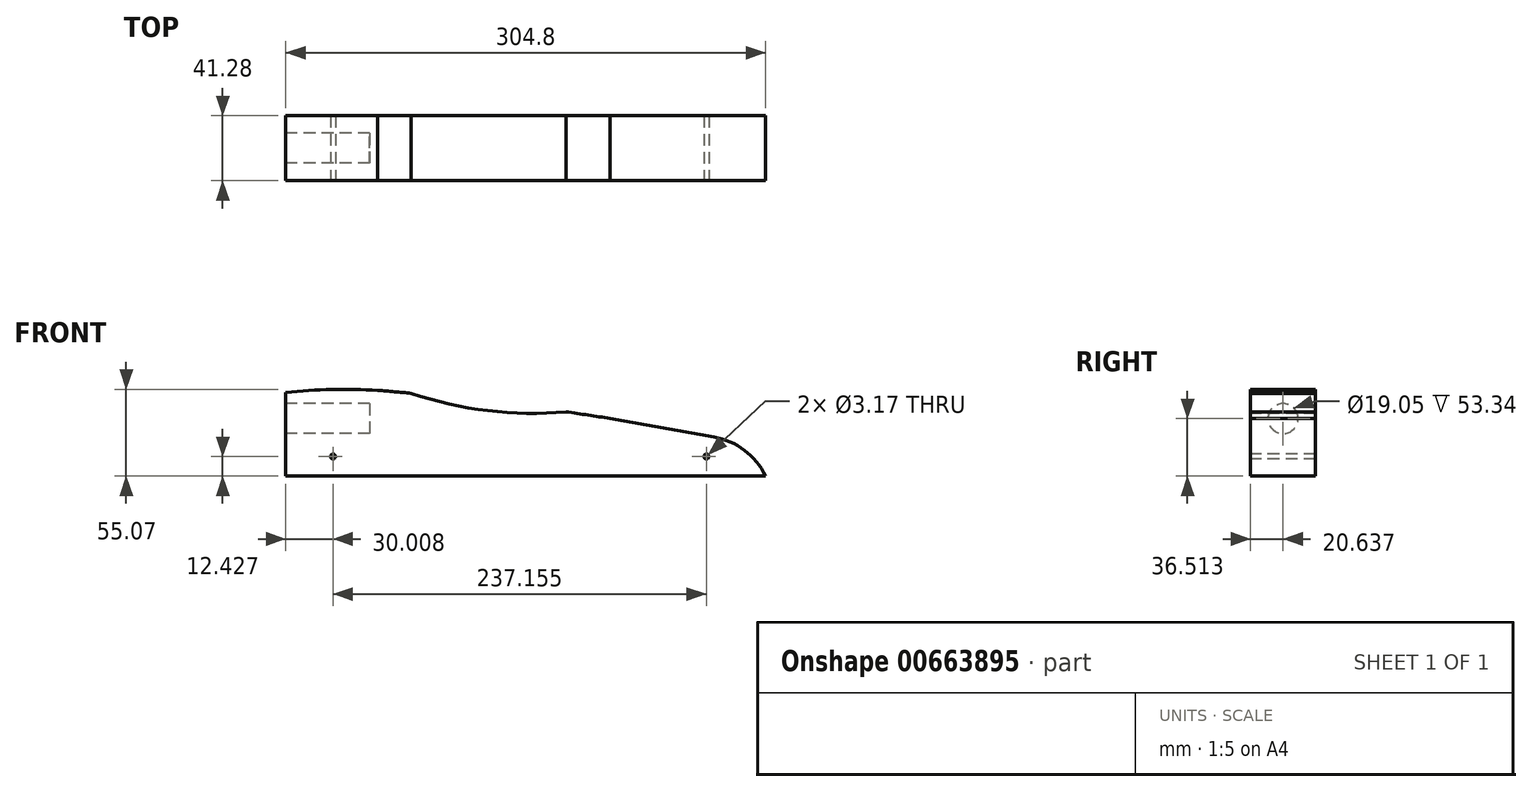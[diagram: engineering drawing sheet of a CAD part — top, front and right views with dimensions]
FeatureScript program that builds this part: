
annotation { "Feature Type Name" : "Feature", "Feature Type Description" : "" }
export const myFeature = defineFeature(function(context is Context, id is Id, definition is map)
    precondition{}
    {
        {
            var Q0;
            Q0=qCreatedBy(makeId("Front.planeOp"),FACE);
            var sketch = newSketch(context, id + "F0", { "sketchPlane" : qUnion([Q0])});
            skLineSegment(sketch, "E0", {"start": v(304.8, 19.05) * mm, "end": v(0, 73.03) * mm});
            skLineSegment(sketch, "E1", {"start": v(0, 73.03) * mm, "end": v(0, 0) * mm});
            skLineSegment(sketch, "E2", {"start": v(0, 0) * mm, "end": v(304.8, 0) * mm});
            skLineSegment(sketch, "E3", {"start": v(304.8, 0) * mm, "end": v(304.8, 19.05) * mm});
            skSolve(sketch);
        }
        {
            var Q0;
            Q0=makeQuery(id+"F0.imprint","IMPRINT",FACE,{"disambiguationData":[TD([[makeQuery(id+"F0.imprint","IMPRINT",EDGE,{"derivedFrom":sQuery(id+"F0.wireOp",EDGE,"E0")}),1.0]])]});
            extrude(context, id + "F1", {"entities" : qUnion([Q0]), "oppositeDirection" : true, "depth" : 41.27 * mm, "offsetDistance" : 25.4 * mm});
        }
        {
            var Q0;
            Q0=makeQuery(id+"F1.opExtrude","SWEPT_FACE",FACE,{"disambiguationData":[OSD([sQuery(id+"F0.wireOp",EDGE,"E1")])]});
            var sketch = newSketch(context, id + "F2", { "sketchPlane" : qUnion([Q0])});
            skCircle(sketch, "E4", {"center": v(-20.64, 36.51) * mm, "radius": 9.53 * mm});
            skPoint(sketch, "E4.centerSnap0", {"position": v(-20.64, 73.03) * mm});
            skPoint(sketch, "E4.centerSnap1", {"position": v(0, 36.51) * mm});
            skSolve(sketch);
        }
        {
            var Q0;
            Q0=makeQuery(id+"F2.imprint","IMPRINT",FACE,{"disambiguationData":[TD([[makeQuery(id+"F2.imprint","IMPRINT",EDGE,{"derivedFrom":sQuery(id+"F2.wireOp",EDGE,"E4")}),1.0]])]});
            extrude(context, id + "F3", {"entities" : qUnion([Q0]), "operationType" : NewBodyOperationType.REMOVE, "oppositeDirection" : true, "depth" : 53.34 * mm, "offsetDistance" : 25.4 * mm});
        }
        {
            var Q0;
            Q0=makeQuery(id+"F1.opExtrude","CAP_FACE",FACE,{"disambiguationData":[OSD([sQuery(id+"F0.wireOp",EDGE,"E0"),sQuery(id+"F0.wireOp",EDGE,"E1"),sQuery(id+"F0.wireOp",EDGE,"E2"),sQuery(id+"F0.wireOp",EDGE,"E3")])],"isStart":true});
            var sketch = newSketch(context, id + "F4", { "sketchPlane" : qUnion([Q0])});
            skArc(sketch, "E5", {"start": v(271.47, 24.95) * mm, "mid": v(136.32, 46.4) * mm, "end": v(0, 58.43) * mm});
            skArc(sketch, "E6", {"start": v(304.8, 0) * mm, "mid": v(291.14, 16.48) * mm, "end": v(271.47, 24.95) * mm});
            skSolve(sketch);
        }
        {
            var Q0;
            {var subQ0=sQuery(id+"F4.wireOp",EDGE,"E5");var subQ1=makeQuery(id+"F1.opExtrude","CAP_EDGE",EDGE,{"disambiguationData":[OSD([sQuery(id+"F0.wireOp",EDGE,"E1")])],"isStart":true});var subQ2=makeQuery(id+"F4.imprint","INTERSECT",VERTEX,{"derivedFrom":[subQ1,subQ0]});Q0=makeQuery(id+"F4.imprint","IMPRINT",FACE,{"disambiguationData":[TD([[makeQuery(id+"F4.imprint","IMPRINT",EDGE,{"disambiguationData":[TD([[subQ2,1.0]])],"derivedFrom":subQ0}),-1.0]])]});}
            var Q1;
            {var subQ1=makeQuery(id+"F1.opExtrude","CAP_EDGE",EDGE,{"disambiguationData":[OSD([sQuery(id+"F0.wireOp",EDGE,"E3")])],"isStart":true});Q1=makeQuery(id+"F4.imprint","IMPRINT",FACE,{"disambiguationData":[TD([[makeQuery(id+"F4.imprint","IMPRINT",EDGE,{"derivedFrom":subQ1}),1.0]])]});}
            extrude(context, id + "F5", {"entities" : qUnion([Q0, Q1]), "operationType" : NewBodyOperationType.REMOVE, "oppositeDirection" : true, "depth" : 41.66 * mm, "offsetDistance" : 25.4 * mm});
        }
        {
            var Q0;
            Q0=makeQuery(id+"F1.opExtrude","CAP_FACE",FACE,{"disambiguationData":[OSD([sQuery(id+"F0.wireOp",EDGE,"E0"),sQuery(id+"F0.wireOp",EDGE,"E1"),sQuery(id+"F0.wireOp",EDGE,"E2"),sQuery(id+"F0.wireOp",EDGE,"E3")])],"isStart":true});
            var sketch = newSketch(context, id + "F6", { "sketchPlane" : qUnion([Q0])});
            skArc(sketch, "E7", {"start": v(79.69, 52.56) * mm, "mid": v(128.22, 41.55) * mm, "end": v(177.99, 40.81) * mm});
            skArc(sketch, "E8", {"start": v(79.69, 52.56) * mm, "mid": v(39.86, 55.06) * mm, "end": v(0, 53.15) * mm});
            skSolve(sketch);
        }
        {
            var Q0;
            {var subQ0=sQuery(id+"F6.wireOp",EDGE,"E8");var subQ1=makeQuery(id+"F1.opExtrude","CAP_EDGE",EDGE,{"disambiguationData":[OSD([sQuery(id+"F0.wireOp",EDGE,"E1")])],"isStart":true});var subQ2=makeQuery(id+"F6.imprint","INTERSECT",VERTEX,{"derivedFrom":[subQ1,subQ0]});Q0=makeQuery(id+"F6.imprint","IMPRINT",FACE,{"disambiguationData":[TD([[makeQuery(id+"F6.imprint","IMPRINT",EDGE,{"disambiguationData":[TD([[subQ2,1.0]])],"derivedFrom":subQ0}),-1.0]])]});}
            var Q1;
            {var subQ0=sQuery(id+"F6.wireOp",EDGE,"E7");Q1=makeQuery(id+"F6.imprint","IMPRINT",FACE,{"disambiguationData":[TD([[makeQuery(id+"F6.imprint","IMPRINT",EDGE,{"derivedFrom":subQ0}),1.0]])]});}
            extrude(context, id + "F7", {"entities" : qUnion([Q0, Q1]), "operationType" : NewBodyOperationType.REMOVE, "oppositeDirection" : true, "depth" : 42.16 * mm, "offsetDistance" : 25.4 * mm});
        }
        {
            var Q0;
            Q0=makeQuery(id+"F1.opExtrude","CAP_FACE",FACE,{"disambiguationData":[OSD([sQuery(id+"F0.wireOp",EDGE,"E0"),sQuery(id+"F0.wireOp",EDGE,"E1"),sQuery(id+"F0.wireOp",EDGE,"E2"),sQuery(id+"F0.wireOp",EDGE,"E3")])],"isStart":true});
            var sketch = newSketch(context, id + "F8", { "sketchPlane" : qUnion([Q0])});
            skCircle(sketch, "E9", {"center": v(267.16, 12.43) * mm, "radius": 1.59 * mm});
            skCircle(sketch, "E10", {"center": v(30, 12.43) * mm, "radius": 1.59 * mm});
            skSolve(sketch);
        }
        {
            var Q0;
            Q0=makeQuery(id+"F8.imprint","IMPRINT",FACE,{"disambiguationData":[TD([[makeQuery(id+"F8.imprint","IMPRINT",EDGE,{"derivedFrom":sQuery(id+"F8.wireOp",EDGE,"E10")}),1.0]])]});
            var Q1;
            Q1=makeQuery(id+"F8.imprint","IMPRINT",FACE,{"disambiguationData":[TD([[makeQuery(id+"F8.imprint","IMPRINT",EDGE,{"derivedFrom":sQuery(id+"F8.wireOp",EDGE,"E9")}),1.0]])]});
            extrude(context, id + "F9", {"entities" : qUnion([Q0, Q1]), "operationType" : NewBodyOperationType.REMOVE, "oppositeDirection" : true, "depth" : 41.66 * mm, "offsetDistance" : 25.4 * mm});
        }
    });
